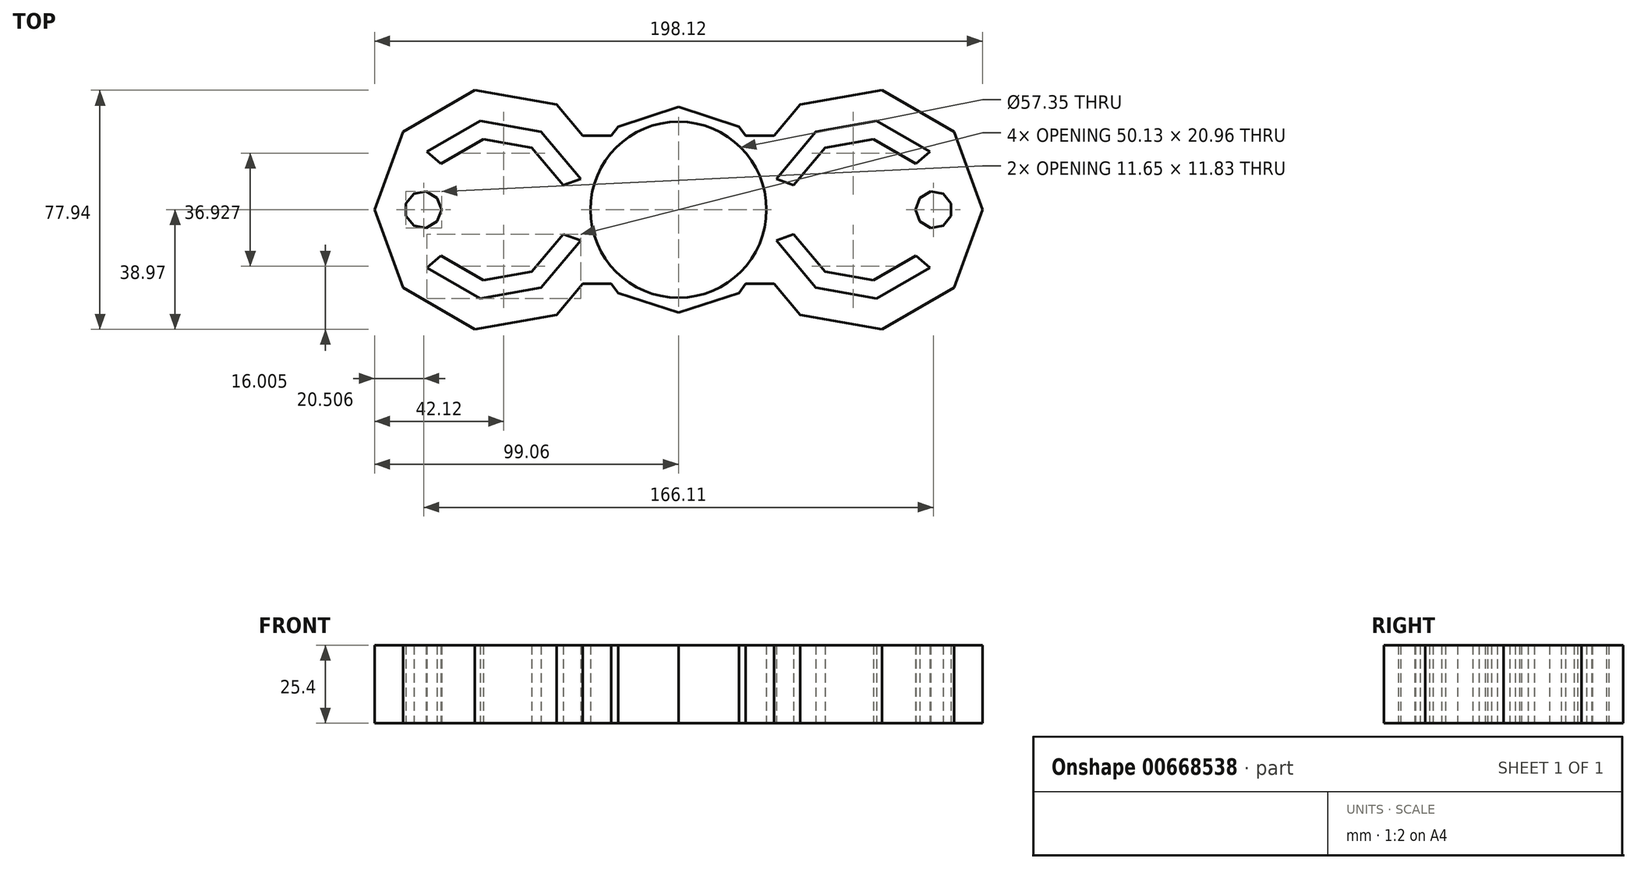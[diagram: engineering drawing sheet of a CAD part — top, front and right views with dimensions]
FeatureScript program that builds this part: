
annotation { "Feature Type Name" : "Feature", "Feature Type Description" : "" }
export const myFeature = defineFeature(function(context is Context, id is Id, definition is map)
    precondition{}
    {
        {
            var Q0;
            Q0=qCreatedBy(makeId("Top.planeOp"),FACE);
            var sketch = newSketch(context, id + "F0", { "sketchPlane" : qUnion([Q0])});
            skLineSegment(sketch, "E0.bottom", {"start": v(46.06, -24.13) * mm, "end": v(43.69, -24.13) * mm});
            skLineSegment(sketch, "E0.top", {"start": v(46.06, 24.13) * mm, "end": v(43.69, 24.13) * mm});
            skLineSegment(sketch, "E0.left", {"start": v(59.5, -24.13) * mm, "end": v(59.5, -21.94) * mm});
            skLineSegment(sketch, "E0.right", {"start": v(-59.5, -24.13) * mm, "end": v(-59.5, -21.94) * mm});
            skPoint(sketch, "E0.middle", {"position": v(0, 0) * mm});
            skLineSegment(sketch, "E1.1", {"start": v(-26.2, -18.17) * mm, "end": v(-39.7, -34.27) * mm});
            skLineSegment(sketch, "E1.2", {"start": v(-39.7, -34.27) * mm, "end": v(-66.36, -38.97) * mm});
            skLineSegment(sketch, "E1.3", {"start": v(-66.36, -38.97) * mm, "end": v(-89.8, -25.43) * mm});
            skLineSegment(sketch, "E1.4", {"start": v(-89.8, -25.43) * mm, "end": v(-99.06, 0) * mm});
            skLineSegment(sketch, "E1.5", {"start": v(-99.06, 0) * mm, "end": v(-89.8, 25.43) * mm});
            skLineSegment(sketch, "E1.6", {"start": v(-89.8, 25.43) * mm, "end": v(-66.36, 38.97) * mm});
            skLineSegment(sketch, "E1.7", {"start": v(-66.36, 38.97) * mm, "end": v(-39.7, 34.27) * mm});
            skLineSegment(sketch, "E1.8", {"start": v(-39.7, 34.27) * mm, "end": v(-26.2, 18.17) * mm});
            skPoint(sketch, "E1.0.midPoint", {"position": v(-22.31, 0) * mm});
            skLineSegment(sketch, "E2.1", {"start": v(22.31, 13.53) * mm, "end": v(24.05, 15.6) * mm});
            skLineSegment(sketch, "E2.2", {"start": v(39.7, 34.27) * mm, "end": v(66.36, 38.97) * mm});
            skLineSegment(sketch, "E2.3", {"start": v(66.36, 38.97) * mm, "end": v(89.8, 25.43) * mm});
            skLineSegment(sketch, "E2.4", {"start": v(89.8, 25.43) * mm, "end": v(99.06, 0) * mm});
            skLineSegment(sketch, "E2.5", {"start": v(99.06, 0) * mm, "end": v(89.8, -25.43) * mm});
            skLineSegment(sketch, "E2.6", {"start": v(89.8, -25.43) * mm, "end": v(66.36, -38.97) * mm});
            skLineSegment(sketch, "E2.7", {"start": v(66.36, -38.97) * mm, "end": v(39.7, -34.27) * mm});
            skLineSegment(sketch, "E2.8", {"start": v(39.7, -34.27) * mm, "end": v(26.2, -18.17) * mm});
            skLineSegment(sketch, "E3.bottom", {"start": v(31.87, 0) * mm, "end": v(-31.87, 0) * mm});
            skLineSegment(sketch, "E3.top", {"start": v(31.87, 0) * mm, "end": v(-31.87, 0) * mm});
            skLineSegment(sketch, "E3.left", {"start": v(31.87, 0) * mm, "end": v(31.87, 0) * mm});
            skLineSegment(sketch, "E3.right", {"start": v(-31.87, 0) * mm, "end": v(-31.87, 0) * mm});
            skArc(sketch, "E4.cCircle", {"start": v(-33.54, 9.45) * mm, "mid": v(-54.7, 27.2) * mm, "end": v(-80.65, 17.75) * mm, "construction": true});
            skLineSegment(sketch, "E4.1", {"start": v(-31.87, -10.05) * mm, "end": v(-44.8, -25.45) * mm});
            skLineSegment(sketch, "E4.2", {"start": v(-44.8, -25.45) * mm, "end": v(-64.6, -28.94) * mm});
            skLineSegment(sketch, "E4.3", {"start": v(-64.6, -28.94) * mm, "end": v(-82, -18.9) * mm});
            skLineSegment(sketch, "E4.6", {"start": v(-82, 18.9) * mm, "end": v(-64.6, 28.94) * mm});
            skLineSegment(sketch, "E4.7", {"start": v(-64.6, 28.94) * mm, "end": v(-44.8, 25.45) * mm});
            skLineSegment(sketch, "E4.8", {"start": v(-44.8, 25.45) * mm, "end": v(-31.87, 10.05) * mm});
            skPoint(sketch, "E4.0.midPoint", {"position": v(-31.87, 0) * mm});
            skArc(sketch, "E5.cCircle", {"start": v(33.54, -9.45) * mm, "mid": v(54.7, -27.2) * mm, "end": v(80.65, -17.75) * mm, "construction": true});
            skLineSegment(sketch, "E5.1", {"start": v(31.87, 10.05) * mm, "end": v(44.8, 25.45) * mm});
            skLineSegment(sketch, "E5.2", {"start": v(44.8, 25.45) * mm, "end": v(64.6, 28.94) * mm});
            skLineSegment(sketch, "E5.3", {"start": v(64.6, 28.94) * mm, "end": v(82, 18.9) * mm});
            skLineSegment(sketch, "E5.6", {"start": v(82, -18.9) * mm, "end": v(64.6, -28.94) * mm});
            skLineSegment(sketch, "E5.7", {"start": v(64.6, -28.94) * mm, "end": v(44.8, -25.45) * mm});
            skLineSegment(sketch, "E5.8", {"start": v(44.8, -25.45) * mm, "end": v(31.87, -10.05) * mm});
            skPoint(sketch, "E5.0.midPoint", {"position": v(31.87, 0) * mm});
            skLineSegment(sketch, "E6.bottom", {"start": v(37.55, 0) * mm, "end": v(-37.55, 0) * mm});
            skLineSegment(sketch, "E6.top", {"start": v(37.55, 0) * mm, "end": v(-37.55, 0) * mm});
            skLineSegment(sketch, "E6.left", {"start": v(37.55, 0) * mm, "end": v(37.55, 0) * mm});
            skLineSegment(sketch, "E6.right", {"start": v(-37.55, 0) * mm, "end": v(-37.55, 0) * mm});
            skArc(sketch, "E7.cCircle", {"start": v(-42.69, 14.1) * mm, "mid": v(-55.68, 21.6) * mm, "end": v(-70.46, 19) * mm, "construction": true});
            skLineSegment(sketch, "E7.1", {"start": v(-37.55, -7.98) * mm, "end": v(-47.82, -20.22) * mm});
            skLineSegment(sketch, "E7.2", {"start": v(-47.82, -20.22) * mm, "end": v(-63.55, -23) * mm});
            skLineSegment(sketch, "E7.3", {"start": v(-63.55, -23) * mm, "end": v(-77.38, -15) * mm});
            skLineSegment(sketch, "E7.6", {"start": v(-77.38, 15) * mm, "end": v(-63.55, 23) * mm});
            skLineSegment(sketch, "E7.7", {"start": v(-63.55, 23) * mm, "end": v(-47.82, 20.22) * mm});
            skLineSegment(sketch, "E7.8", {"start": v(-47.82, 20.22) * mm, "end": v(-37.55, 7.98) * mm});
            skPoint(sketch, "E7.0.midPoint", {"position": v(-37.55, 0) * mm});
            skArc(sketch, "E8.cCircle", {"start": v(42.69, -14.1) * mm, "mid": v(55.68, -21.6) * mm, "end": v(70.46, -19) * mm, "construction": true});
            skLineSegment(sketch, "E8.1", {"start": v(37.55, 7.98) * mm, "end": v(47.82, 20.22) * mm});
            skLineSegment(sketch, "E8.2", {"start": v(47.82, 20.22) * mm, "end": v(63.55, 23) * mm});
            skLineSegment(sketch, "E8.3", {"start": v(63.55, 23) * mm, "end": v(77.38, 15) * mm});
            skLineSegment(sketch, "E8.6", {"start": v(77.38, -15) * mm, "end": v(63.55, -23) * mm});
            skLineSegment(sketch, "E8.7", {"start": v(63.55, -23) * mm, "end": v(47.82, -20.22) * mm});
            skLineSegment(sketch, "E8.8", {"start": v(47.82, -20.22) * mm, "end": v(37.55, -7.98) * mm});
            skPoint(sketch, "E8.0.midPoint", {"position": v(37.55, 0) * mm});
            skLineSegment(sketch, "E9", {"start": v(-37.55, 7.98) * mm, "end": v(-31.87, 10.05) * mm});
            skLineSegment(sketch, "E10", {"start": v(-37.55, -7.98) * mm, "end": v(-31.87, -10.05) * mm});
            skLineSegment(sketch, "E11", {"start": v(-77.38, -15) * mm, "end": v(-82, -18.9) * mm});
            skLineSegment(sketch, "E12", {"start": v(-77.38, 15) * mm, "end": v(-82, 18.9) * mm});
            skLineSegment(sketch, "E13", {"start": v(37.55, 7.98) * mm, "end": v(31.87, 10.05) * mm});
            skLineSegment(sketch, "E14", {"start": v(37.55, -7.98) * mm, "end": v(31.87, -10.05) * mm});
            skLineSegment(sketch, "E15", {"start": v(77.38, 15) * mm, "end": v(82, 18.9) * mm});
            skLineSegment(sketch, "E16", {"start": v(77.38, -15) * mm, "end": v(82, -18.9) * mm});
            skArc(sketch, "E17.trimOffspring", {"start": v(70.46, 19) * mm, "mid": v(55.68, 21.6) * mm, "end": v(42.69, 14.1) * mm, "construction": true});
            skArc(sketch, "E18.trimOffspring", {"start": v(80.65, 17.75) * mm, "mid": v(54.7, 27.2) * mm, "end": v(33.54, 9.45) * mm, "construction": true});
            skPoint(sketch, "E19.orphan", {"position": v(88.88, 0) * mm});
            skArc(sketch, "E20.trimOffspring", {"start": v(-80.65, -17.75) * mm, "mid": v(-54.7, -27.2) * mm, "end": v(-33.54, -9.45) * mm, "construction": true});
            skArc(sketch, "E21.trimOffspring", {"start": v(-70.46, -19) * mm, "mid": v(-55.68, -21.6) * mm, "end": v(-42.69, -14.1) * mm, "construction": true});
            skPoint(sketch, "E22.orphan", {"position": v(-88.88, 0) * mm});
            skLineSegment(sketch, "E23.bottom", {"start": v(83.24, 0) * mm, "end": v(-83.24, 0) * mm});
            skLineSegment(sketch, "E23.top", {"start": v(83.24, 0) * mm, "end": v(-83.24, 0) * mm});
            skLineSegment(sketch, "E23.left", {"start": v(83.24, 0) * mm, "end": v(83.24, 0) * mm});
            skLineSegment(sketch, "E23.right", {"start": v(-83.24, 0) * mm, "end": v(-83.24, 0) * mm});
            skCircle(sketch, "E24.cCircle", {"center": v(-83.24, 0) * mm, "radius": 5.64 * mm, "construction": true});
            skLineSegment(sketch, "E24.0", {"start": v(-88.88, -2.05) * mm, "end": v(-88.88, 2.05) * mm});
            skLineSegment(sketch, "E24.1", {"start": v(-88.88, 2.05) * mm, "end": v(-86.24, 5.2) * mm});
            skLineSegment(sketch, "E24.2", {"start": v(-86.24, 5.2) * mm, "end": v(-82.2, 5.91) * mm});
            skLineSegment(sketch, "E24.3", {"start": v(-82.2, 5.91) * mm, "end": v(-78.64, 3.86) * mm});
            skLineSegment(sketch, "E24.4", {"start": v(-78.64, 3.86) * mm, "end": v(-77.23, 0) * mm});
            skLineSegment(sketch, "E24.5", {"start": v(-77.23, 0) * mm, "end": v(-78.64, -3.86) * mm});
            skLineSegment(sketch, "E24.6", {"start": v(-78.64, -3.86) * mm, "end": v(-82.2, -5.91) * mm});
            skLineSegment(sketch, "E24.7", {"start": v(-82.2, -5.91) * mm, "end": v(-86.24, -5.2) * mm});
            skLineSegment(sketch, "E24.8", {"start": v(-86.24, -5.2) * mm, "end": v(-88.88, -2.05) * mm});
            skCircle(sketch, "E25.cCircle", {"center": v(83.24, 0) * mm, "radius": 5.64 * mm, "construction": true});
            skLineSegment(sketch, "E25.0", {"start": v(88.88, 2.05) * mm, "end": v(88.88, -2.05) * mm});
            skLineSegment(sketch, "E25.1", {"start": v(88.88, -2.05) * mm, "end": v(86.24, -5.2) * mm});
            skLineSegment(sketch, "E25.2", {"start": v(86.24, -5.2) * mm, "end": v(82.2, -5.91) * mm});
            skLineSegment(sketch, "E25.3", {"start": v(82.2, -5.91) * mm, "end": v(78.64, -3.86) * mm});
            skLineSegment(sketch, "E25.4", {"start": v(78.64, -3.86) * mm, "end": v(77.23, 0) * mm});
            skLineSegment(sketch, "E25.5", {"start": v(77.23, 0) * mm, "end": v(78.64, 3.86) * mm});
            skLineSegment(sketch, "E25.6", {"start": v(78.64, 3.86) * mm, "end": v(82.2, 5.91) * mm});
            skLineSegment(sketch, "E25.7", {"start": v(82.2, 5.91) * mm, "end": v(86.24, 5.2) * mm});
            skLineSegment(sketch, "E25.8", {"start": v(86.24, 5.2) * mm, "end": v(88.88, 2.05) * mm});
            skEllipticalArc(sketch, "E26", {});
            skCircle(sketch, "E27", {"center": v(0, 0) * mm, "radius": 28.67 * mm});
            skLineSegment(sketch, "E28.1", {"start": v(31.87, -10.36) * mm, "end": v(19.7, -27.11) * mm});
            skLineSegment(sketch, "E28.2", {"start": v(19.7, -27.11) * mm, "end": v(0, -33.52) * mm});
            skLineSegment(sketch, "E28.3", {"start": v(0, -33.52) * mm, "end": v(-19.7, -27.11) * mm});
            skLineSegment(sketch, "E28.4", {"start": v(-19.7, -27.11) * mm, "end": v(-31.87, -10.36) * mm});
            skLineSegment(sketch, "E28.6", {"start": v(-31.87, 10.36) * mm, "end": v(-19.7, 27.11) * mm});
            skLineSegment(sketch, "E28.7", {"start": v(-19.7, 27.11) * mm, "end": v(0, 33.52) * mm});
            skLineSegment(sketch, "E28.8", {"start": v(0, 33.52) * mm, "end": v(19.7, 27.11) * mm});
            skLineSegment(sketch, "E28.9", {"start": v(19.7, 27.11) * mm, "end": v(31.87, 10.36) * mm});
            skEllipticalArc(sketch, "E29.trimOffspring", {});
            skPoint(sketch, "E30.orphan", {"position": v(-22.31, -13.53) * mm});
            skLineSegment(sketch, "E31", {"start": v(-31.87, 10.05) * mm, "end": v(-31.87, -10.05) * mm});
            skLineSegment(sketch, "E32", {"start": v(31.87, 10.36) * mm, "end": v(31.87, -10.05) * mm});
            skLineSegment(sketch, "E33.trimOffspring", {"start": v(26.2, 18.17) * mm, "end": v(39.7, 34.27) * mm});
            skLineSegment(sketch, "E34.trimOffspring", {"start": v(-24.05, 15.6) * mm, "end": v(-22.31, 13.53) * mm});
            skLineSegment(sketch, "E35.trimOffspring", {"start": v(24.05, -15.6) * mm, "end": v(22.31, -13.53) * mm});
            skLineSegment(sketch, "E36.trimOffspring", {"start": v(-59.5, 21.94) * mm, "end": v(-59.5, 24.13) * mm});
            skLineSegment(sketch, "E37.trimOffspring", {"start": v(59.5, 21.94) * mm, "end": v(59.5, 24.13) * mm});
            skLineSegment(sketch, "E38.trimOffspring", {"start": v(31.2, 24.13) * mm, "end": v(21.87, 24.13) * mm});
            skLineSegment(sketch, "E39.trimOffspring", {"start": v(31.2, -24.13) * mm, "end": v(21.87, -24.13) * mm});
            skLineSegment(sketch, "E40.trimOffspring", {"start": v(15.49, -24.13) * mm, "end": v(-15.49, -24.13) * mm});
            skLineSegment(sketch, "E41.trimOffspring", {"start": v(-21.87, -24.13) * mm, "end": v(-59.5, -24.13) * mm});
            skLineSegment(sketch, "E42.trimOffspring", {"start": v(-21.87, 24.13) * mm, "end": v(-59.5, 24.13) * mm});
            skLineSegment(sketch, "E43.trimOffspring", {"start": v(15.49, 24.13) * mm, "end": v(-15.49, 24.13) * mm});
            const initialGuessF0  = {"E26": [0, 0, 1, 0, 0.026971114799380302, 0.010435148743837663, 2.486357788852112, 2.5449232941753617], "E29.trimOffspring": [0, 0, 1, 0, 0.026971114799380302, 0.010435148743837663, 3.709531884465227, 3.796827518327473]};
            skSetInitialGuess(sketch, initialGuessF0);
            skSolve(sketch);
        }
        {
            var Q0;
            Q0 = qSketchRegion(id + "F0", true);
            extrude(context, id + "F1", {"entities" : qUnion([Q0]), "depth" : 25.4 * mm, "offsetDistance" : 25.4 * mm});
        }
        {
            var Q0;
            Q0 = qSketchRegion(id + "F0", true);
            extrude(context, id + "F2", {"entities" : qUnion([Q0]), "operationType" : NewBodyOperationType.ADD, "depth" : 25.4 * mm, "offsetDistance" : 25.4 * mm});
        }
        {
            var Q0;
            Q0 = qSketchRegion(id + "F0", true);
            extrude(context, id + "F3", {"entities" : qUnion([Q0]), "operationType" : NewBodyOperationType.ADD, "depth" : 25.4 * mm, "offsetDistance" : 25.4 * mm});
        }
    });
